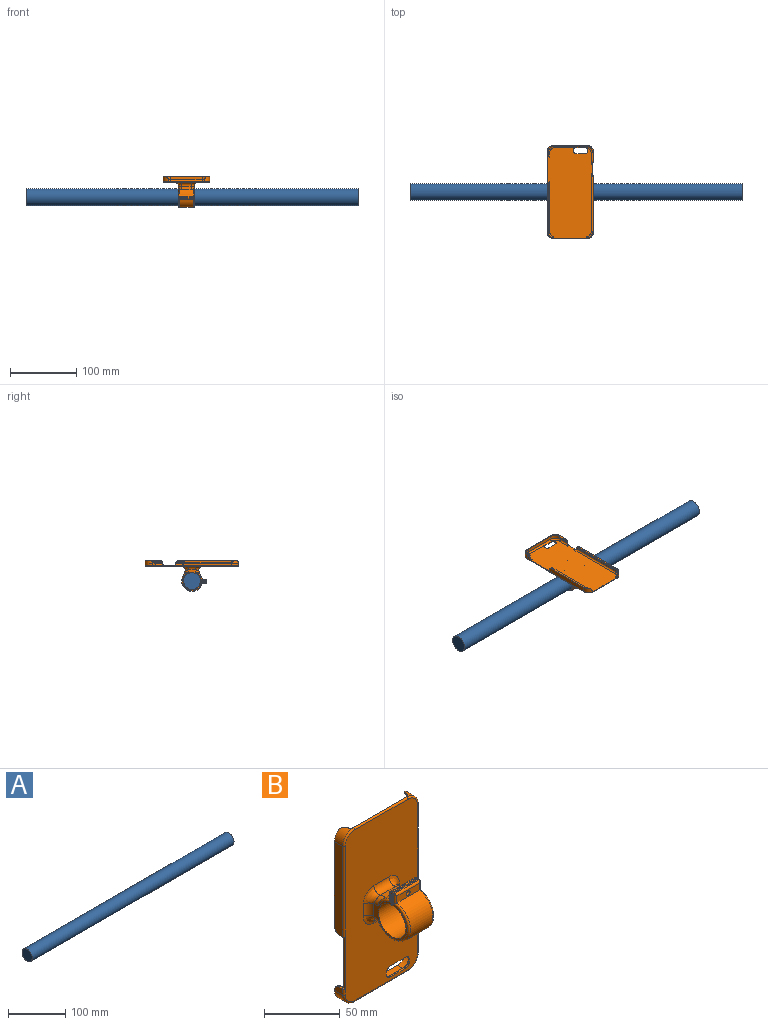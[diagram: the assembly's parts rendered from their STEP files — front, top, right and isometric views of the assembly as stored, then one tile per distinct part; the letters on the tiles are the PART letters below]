
ASSEMBLY  parts=2 mates=1
PART A: 3 faces, bbox 500x25.4x25.4 mm
  f0: cylinder r=12.7mm len=500mm, axis (-1,0,0), area 39898.2mm2, adj f1,f2
  f1: plane 25.4x25.4mm, normal (1,0,0), area 506.7mm2, adj f0
  f2: plane 25.4x25.4mm, normal (-1,0,0), area 506.7mm2, adj f0
PART B: 121 faces, bbox 71.8x47.8x142.4 mm
  f0: plane 138.18x67.56mm, normal (0,-1,0), area 8144.3mm2, adj f1,f2,f23,f24,f25,f26,f39,f40
  f1: cylinder r=1.27mm len=5.08mm, axis (0,0,1), area 10.1mm2, adj f0,f4,f17,f43
  f2: cylinder r=1.27mm len=84.84mm, axis (0,0,-1), area 169.2mm2, adj f0,f3,f19,f50
  f3: plane 84.84x7.62mm, normal (1,0,0), area 641.1mm2, adj f2,f10,f19,f33,f72
  f4: plane 7.62x5.08mm, normal (-1,0,0), area 33.3mm2, adj f1,f14,f17,f31,f75
  f5: plane 72.88x2.54mm, normal (1,0,0), area 184.6mm2, adj f18,f27,f53,f63,f74
  f6: plane 84.31x2.54mm, normal (-1,0,0), area 213.6mm2, adj f19,f28,f51,f62,f72
  f7: plane 15.24x2.54mm, normal (-1,0,0), area 38.2mm2, adj f20,f29,f59,f64,f73
  f8: plane 3.81x2.54mm, normal (1,0,0), area 9.2mm2, adj f17,f30,f55,f65,f75
  f9: plane 75.22x2.62mm, normal (0,1,0), area 182.5mm2, adj f13,f27,f34,f38,f67,f71,f74
  f10: plane 86.65x2.62mm, normal (0,1,0), area 211.5mm2, adj f3,f28,f33,f37,f66,f70,f72
  f11: plane 16.51x7.62mm, normal (1,0,0), area 120.4mm2, adj f14,f20,f32,f48,f73
  f12: plane 49.78x7.62mm, normal (0,0,-1), area 379.4mm2, adj f14,f31,f32,f44
  f13: plane 73.41x7.62mm, normal (-1,0,0), area 554mm2, adj f9,f18,f34,f45,f74
  f14: plane 70.1x21.67mm, normal (0,1,0), area 140.5mm2, adj f4,f11,f12,f15,f29,f30,f31,f32
  f15: plane 47.24x5.08mm, normal (0,0,1), area 240mm2, adj f14,f29,f30,f57
  f16: plane 136.91x67.56mm, normal (0,1,0), area 8415.3mm2, adj f23,f25,f26,f39,f40,f41,f42,f49
  f17: plane 3.89x1.27mm, normal (0,0,1), area 4.6mm2, adj f1,f4,f8,f61,f75
  f18: plane 3.89x1.27mm, normal (0,0,-1), area 4.6mm2, adj f5,f13,f45,f61,f74
  f19: plane 3.89x1.27mm, normal (0,0,-1), area 4.6mm2, adj f2,f3,f6,f60,f72
  f20: plane 3.89x1.27mm, normal (0,0,1), area 4.6mm2, adj f7,f11,f48,f60,f73
  f21: plane 0.95x0.08mm, normal (1,0,0), area 0.1mm2, adj f27,f34,f71,f76
  f22: plane 0.95x0.08mm, normal (-1,0,0), area 0.1mm2, adj f28,f33,f70,f77
  f23: plane 1.27x1.27mm, normal (-1,0,0), area 1.6mm2, adj f0,f16,f39,f40
  f24: plane 13.97x1.27mm, normal (0,0,1), area 17.7mm2, adj f0,f40,f41,f57
  f25: plane 1.27x1.27mm, normal (1,0,0), area 1.6mm2, adj f0,f16,f41,f42
  f26: plane 13.97x1.27mm, normal (0,0,-1), area 17.7mm2, adj f0,f16,f39,f42
  f27: cylinder r=10.16mm len=9.42mm, axis (0,1,0), area 49.3mm2, adj f5,f9,f21,f54,f63,f67,f71
  f28: cylinder r=10.16mm len=9.42mm, axis (0,-1,0), area 49.3mm2, adj f6,f10,f22,f52,f62,f66,f70
  f29: cylinder r=10.16mm len=10.16mm, axis (0,1,0), area 75.4mm2, adj f7,f14,f15,f58,f64,f68
  f30: cylinder r=10.16mm len=10.16mm, axis (0,1,0), area 75.4mm2, adj f8,f14,f15,f56,f65,f69
  f31: cylinder r=10.16mm len=10.16mm, axis (0,-1,0), area 121.6mm2, adj f4,f12,f14,f43
  f32: cylinder r=10.16mm len=10.16mm, axis (0,-1,0), area 121.6mm2, adj f11,f12,f14,f46
  f33: cylinder r=10.16mm len=10.16mm, axis (0,-1,0), area 97.7mm2, adj f3,f10,f22,f50,f70,f77
  f34: cylinder r=10.16mm len=10.16mm, axis (0,-1,0), area 97.7mm2, adj f9,f13,f21,f47,f71,f76
  f35: plane 2.14x1.13mm, normal (1,0,0), area 1.4mm2, adj f65,f69,f75
  f36: plane 13.57x1.27mm, normal (-1,0,0), area 15.9mm2, adj f14,f64,f68,f73
  f37: plane 82.64x1.27mm, normal (-1,0,0), area 103.6mm2, adj f10,f62,f66,f72
  f38: plane 71.21x1.27mm, normal (1,0,0), area 89.1mm2, adj f9,f63,f67,f74
  f39: cylinder r=3.81mm len=3.81mm, axis (0,1,0), area 7.6mm2, adj f0,f16,f23,f26
  f40: cylinder r=3.81mm len=3.81mm, axis (0,1,0), area 7.6mm2, adj f0,f16,f23,f24
  f41: cylinder r=3.81mm len=3.81mm, axis (0,1,0), area 7.6mm2, adj f0,f16,f24,f25
  f42: cylinder r=3.81mm len=3.81mm, axis (0,1,0), area 7.6mm2, adj f0,f16,f25,f26
  f43: torus R=8.89mm, axis (0,1,0), area 30.4mm2, adj f0,f1,f31,f44
  f44: cylinder r=1.27mm len=49.78mm, axis (-1,0,0), area 99.3mm2, adj f0,f12,f43,f46
  f45: cylinder r=1.27mm len=73.41mm, axis (0,0,1), area 146.4mm2, adj f0,f13,f18,f47
  f46: torus R=8.89mm, axis (0,1,0), area 30.4mm2, adj f0,f32,f44,f48
  f47: torus R=8.89mm, axis (0,1,0), area 30.4mm2, adj f0,f34,f45,f49
  f48: cylinder r=1.27mm len=16.51mm, axis (0,0,-1), area 32.9mm2, adj f0,f11,f20,f46
  f49: cylinder r=1.27mm len=49.78mm, axis (1,0,0), area 99.3mm2, adj f0,f16,f47,f50
  f50: torus R=8.89mm, axis (0,1,0), area 30.4mm2, adj f0,f2,f33,f49
  f51: cylinder r=2.54mm len=86.85mm, axis (0,0,1), area 340.1mm2, adj f6,f16,f52,f78
  f52: torus R=7.62mm, axis (0,1,0), area 46.2mm2, adj f16,f28,f51,f77
  f53: cylinder r=2.54mm len=75.42mm, axis (0,0,-1), area 294.5mm2, adj f5,f16,f54,f80
  f54: torus R=7.62mm, axis (0,1,0), area 46.2mm2, adj f16,f27,f53,f76
  f55: cylinder r=2.54mm len=6.35mm, axis (0,0,-1), area 18.9mm2, adj f8,f16,f56,f81
  f56: torus R=7.62mm, axis (0,1,0), area 57.9mm2, adj f16,f30,f55,f57
  f57: cylinder r=2.54mm len=47.24mm, axis (1,0,0), area 188.5mm2, adj f15,f16,f24,f56,f58
  f58: torus R=7.62mm, axis (0,1,0), area 57.9mm2, adj f16,f29,f57,f59
  f59: cylinder r=2.54mm len=17.78mm, axis (0,0,1), area 64.5mm2, adj f7,f16,f58,f79
  f60: plane 19.05x3.81mm, normal (1,0,0), area 27mm2, adj f0,f16,f19,f20,f78,f79
  f61: plane 41.91x3.81mm, normal (-1,0,0), area 56mm2, adj f0,f16,f17,f18,f80,f81
  f62: cylinder r=1.27mm len=86.35mm, axis (0,0,1), area 167.4mm2, adj f6,f28,f37,f66,f72
  f63: cylinder r=1.27mm len=74.92mm, axis (0,0,-1), area 144.6mm2, adj f5,f27,f38,f67,f74
  f64: cylinder r=1.27mm len=17.28mm, axis (0,0,1), area 29.7mm2, adj f7,f29,f36,f68,f73
  f65: cylinder r=1.27mm len=5.85mm, axis (0,0,-1), area 6.9mm2, adj f8,f30,f35,f69,f75
  f66: cylinder r=2.54mm len=2.69mm, axis (0,1,0), area 4.7mm2, adj f10,f28,f37,f62
  f67: cylinder r=2.54mm len=2.69mm, axis (0,-1,0), area 4.7mm2, adj f9,f27,f38,f63
  f68: cylinder r=2.54mm len=2.69mm, axis (0,-1,0), area 4.7mm2, adj f14,f29,f36,f64
  f69: cylinder r=2.54mm len=2.69mm, axis (0,1,0), area 4.6mm2, adj f14,f30,f35,f65,f75
  f70: cylinder r=5mm len=5.31mm, axis (0,0,1), area 10.3mm2, adj f10,f22,f28,f33
  f71: cylinder r=5mm len=5.31mm, axis (0,0,1), area 10.3mm2, adj f9,f21,f27,f34
  f72: cylinder r=5mm len=5mm, axis (1,0,0), area 15.1mm2, adj f3,f6,f10,f19,f37,f62
  f73: cylinder r=5mm len=5mm, axis (1,0,0), area 15.1mm2, adj f7,f11,f14,f20,f36,f64
  f74: cylinder r=5mm len=5mm, axis (-1,0,0), area 15.1mm2, adj f5,f9,f13,f18,f38,f63
  f75: cylinder r=5mm len=5mm, axis (-1,0,0), area 14.6mm2, adj f4,f8,f14,f17,f35,f65,f69
  f76: cylinder r=2.54mm len=3.18mm, axis (0,0,1), area 7.1mm2, adj f16,f21,f34,f54
  f77: cylinder r=2.54mm len=3.18mm, axis (0,0,1), area 7.1mm2, adj f16,f22,f33,f52
  f78: cylinder r=2.54mm len=2.54mm, axis (1,0,0), area 3.7mm2, adj f16,f51,f60
  f79: cylinder r=2.54mm len=2.54mm, axis (1,0,0), area 3.7mm2, adj f16,f59,f60
  f80: cylinder r=2.54mm len=2.54mm, axis (-1,0,0), area 3.7mm2, adj f16,f53,f61
  f81: cylinder r=2.54mm len=2.54mm, axis (-1,0,0), area 3.7mm2, adj f16,f55,f61
  f82: plane 21x5.5mm, normal (0,-1,0), area 105.9mm2, adj f83,f111,f112,f113,f119
  f83: cylinder r=15.6mm len=30.91mm, axis (-1,0,0), area 1215.8mm2, adj f82,f84,f97,f98,f109,f110
  f84: plane 14x5.37mm, normal (0,0.21,-0.98), area 76.9mm2, adj f83,f97,f98,f99
  f85: plane 14x5.29mm, normal (0,0.21,0.98), area 75.6mm2, adj f86,f103,f104,f108
  f86: cylinder r=15.6mm len=21mm, axis (-1,0,0), area 189.1mm2, adj f85,f87,f103,f104,f114,f115
  f87: plane 21x5.5mm, normal (0,1,0), area 105.9mm2, adj f86,f116,f117,f118,f120
  f88: plane 24x1mm, normal (0,0,1), area 24mm2, adj f89,f95,f96,f118
  f89: plane 24x10mm, normal (0,-1,0), area 230.4mm2, adj f88,f90,f95,f96,f120
  f90: plane 24x2.5mm, normal (0,0,-1), area 60mm2, adj f89,f91,f95,f96
  f91: cylinder r=12.7mm len=25.4mm, axis (-1,0,0), area 1769.7mm2, adj f90,f92,f95,f96
  f92: plane 24x2.5mm, normal (0,0,-1), area 60mm2, adj f91,f93,f95,f96
  f93: plane 24x10mm, normal (0,1,0), area 230.4mm2, adj f92,f94,f95,f96,f119
  f94: plane 24x1mm, normal (0,0,1), area 24mm2, adj f93,f95,f96,f113
  f95: plane 36.41x31.1mm, normal (1,0,0), area 169mm2, adj f88,f89,f90,f91,f92,f93,f94,f97
  f96: plane 36.41x31.1mm, normal (-1,0,0), area 169mm2, adj f88,f89,f90,f91,f92,f93,f94,f98
  f97: cylinder r=5mm len=8.49mm, axis (0,-0.98,-0.21), area 34.7mm2, adj f83,f84,f95,f100,f109
  f98: cylinder r=5mm len=8.49mm, axis (0,0.98,0.21), area 34.7mm2, adj f83,f84,f96,f101,f110
  f99: cylinder r=5mm len=14mm, axis (-1,0,0), area 124.6mm2, adj f0,f84,f100,f101
  f100: bspline ~12x10mm, area 90.8mm2, adj f0,f97,f99,f102
  f101: bspline ~11.74x10.67mm, area 90.8mm2, adj f0,f98,f99,f105
  f102: cylinder r=5mm len=9.9mm, axis (0,0,1), area 77.8mm2, adj f0,f95,f100,f106
  f103: cylinder r=5mm len=8.4mm, axis (0,0.98,-0.21), area 34.3mm2, adj f85,f86,f95,f106,f114
  f104: cylinder r=5mm len=8.4mm, axis (0,-0.98,0.21), area 34.3mm2, adj f85,f86,f96,f107,f115
  f105: cylinder r=5mm len=9.9mm, axis (0,0,-1), area 77.8mm2, adj f0,f96,f101,f107
  f106: bspline ~11.74x10.67mm, area 90.8mm2, adj f0,f102,f103,f108
  f107: bspline ~12x10mm, area 90.8mm2, adj f0,f104,f105,f108
  f108: cylinder r=5mm len=14mm, axis (1,0,0), area 124.6mm2, adj f0,f85,f106,f107
  f109: torus R=14.1mm, axis (1,0,0), area 141.8mm2, adj f83,f95,f97,f111
  f110: torus R=14.1mm, axis (1,0,0), area 141.8mm2, adj f83,f96,f98,f112
  f111: cylinder r=1.5mm len=8.29mm, axis (0,0,1), area 16.3mm2, adj f82,f95,f109,f113
  f112: cylinder r=1.5mm len=8.29mm, axis (0,0,-1), area 16.3mm2, adj f82,f96,f110,f113
  f113: cylinder r=1.5mm len=24mm, axis (-1,0,0), area 54mm2, adj f82,f94,f111,f112
  f114: torus R=14.1mm, axis (1,0,0), area 30.6mm2, adj f86,f95,f103,f116
  f115: torus R=14.1mm, axis (1,0,0), area 30.6mm2, adj f86,f96,f104,f117
  f116: cylinder r=1.5mm len=8.29mm, axis (0,0,-1), area 16.3mm2, adj f87,f95,f114,f118
  f117: cylinder r=1.5mm len=8.29mm, axis (0,0,1), area 16.3mm2, adj f87,f96,f115,f118
  f118: cylinder r=1.5mm len=24mm, axis (-1,0,0), area 54mm2, adj f87,f88,f116,f117
  f119: cylinder r=1.75mm len=3.5mm, axis (0,-1,0), area 27.5mm2, adj f82,f93
  f120: cylinder r=1.75mm len=3.5mm, axis (0,-1,0), area 27.5mm2, adj f87,f89
PLACE A at identity
PLACE B rot(axis=(1,0,0),90deg) t=(-8.44,0,22)mm
MATE slider A.f0 <-> B.f91  axis (-1,0,0) through (0,0,0)mm
